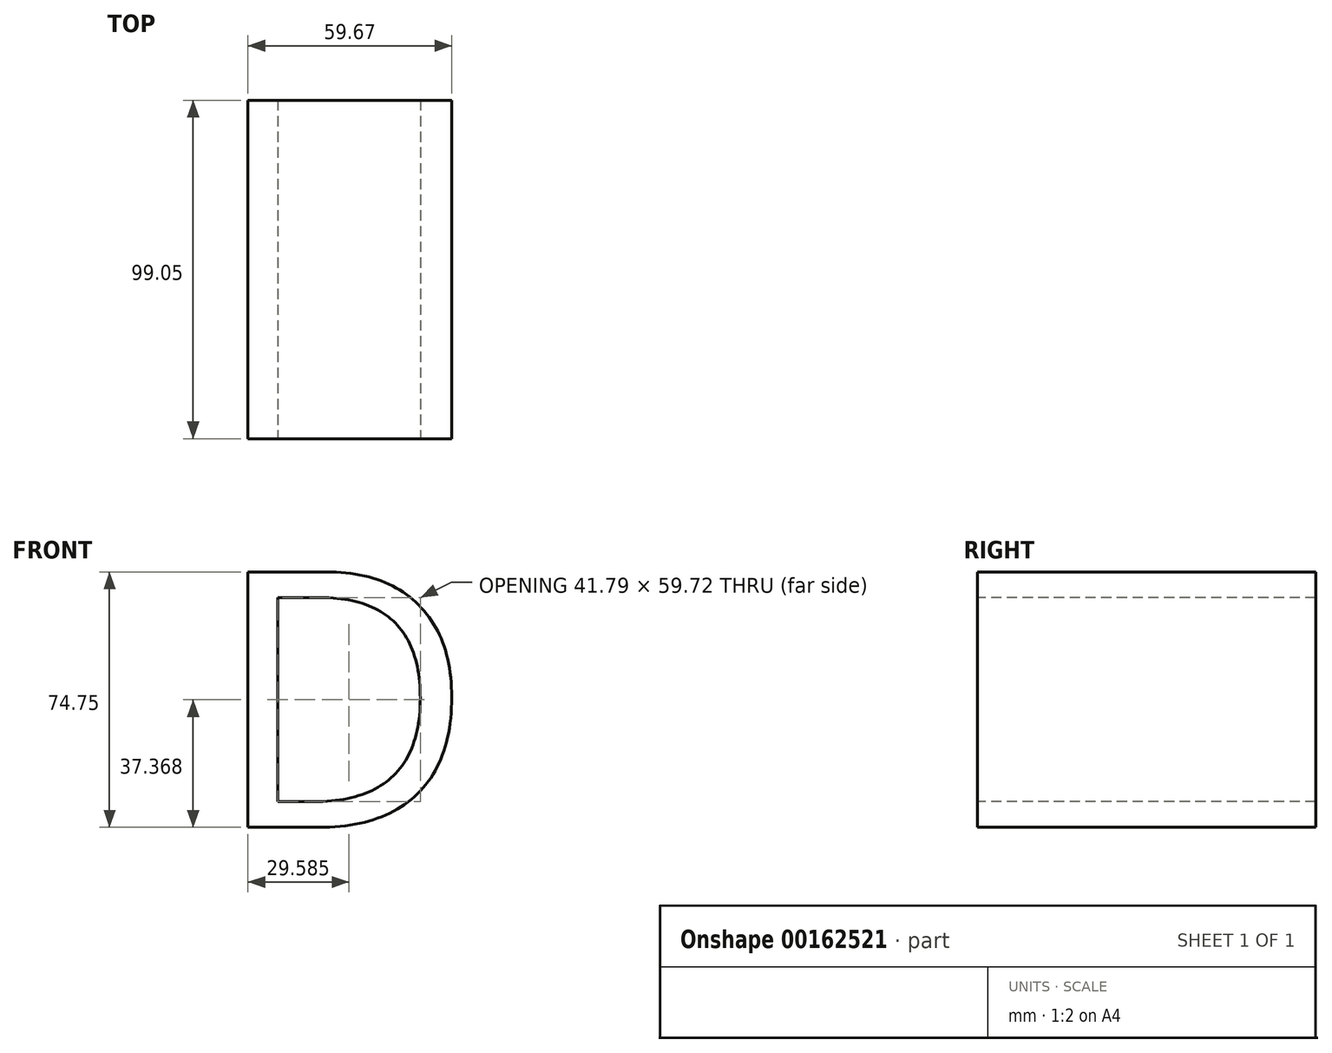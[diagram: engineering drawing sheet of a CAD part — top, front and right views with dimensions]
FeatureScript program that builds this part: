
annotation { "Feature Type Name" : "Feature", "Feature Type Description" : "" }
export const myFeature = defineFeature(function(context is Context, id is Id, definition is map)
    precondition{}
    {
        {
            var Q0;
            Q0=qCreatedBy(makeId("Front.planeOp"),FACE);
            var sketch = newSketch(context, id + "F0", { "sketchPlane" : qUnion([Q0])});
            skText(sketch, "E0", { "text": "D", "fontName": "OpenSans-Regular.ttf"});
            const initialGuessF0  = {"E0": [0, 0, 1, 0, 0.07539]};
            skSetInitialGuess(sketch, initialGuessF0);
            skSolve(sketch);
        }
        {
            var Q0;
            Q0=qCreatedBy(makeId("Right.planeOp"),FACE);
            var sketch = newSketch(context, id + "F1", { "sketchPlane" : qUnion([Q0])});
            skText(sketch, "E1", { "text": "B", "fontName": "OpenSans-Regular.ttf"});
            const initialGuessF1  = {"E1": [0, 0, 1, 0, 0.07539]};
            skSetInitialGuess(sketch, initialGuessF1);
            skSolve(sketch);
        }
        {
            var Q0;
            Q0=makeQuery(id+"F0.imprint","IMPRINT",FACE,{"disambiguationData":[TD([[makeQuery(id+"F0.imprint","IMPRINT",EDGE,{"derivedFrom":sQuery(id+"F0.wireOp",EDGE,"E0.sketch_text.stroke-0")}),-1.0]])]});
            extrude(context, id + "F2", {"entities" : qUnion([Q0]), "oppositeDirection" : true, "depth" : 99.05 * mm});
        }
    });
